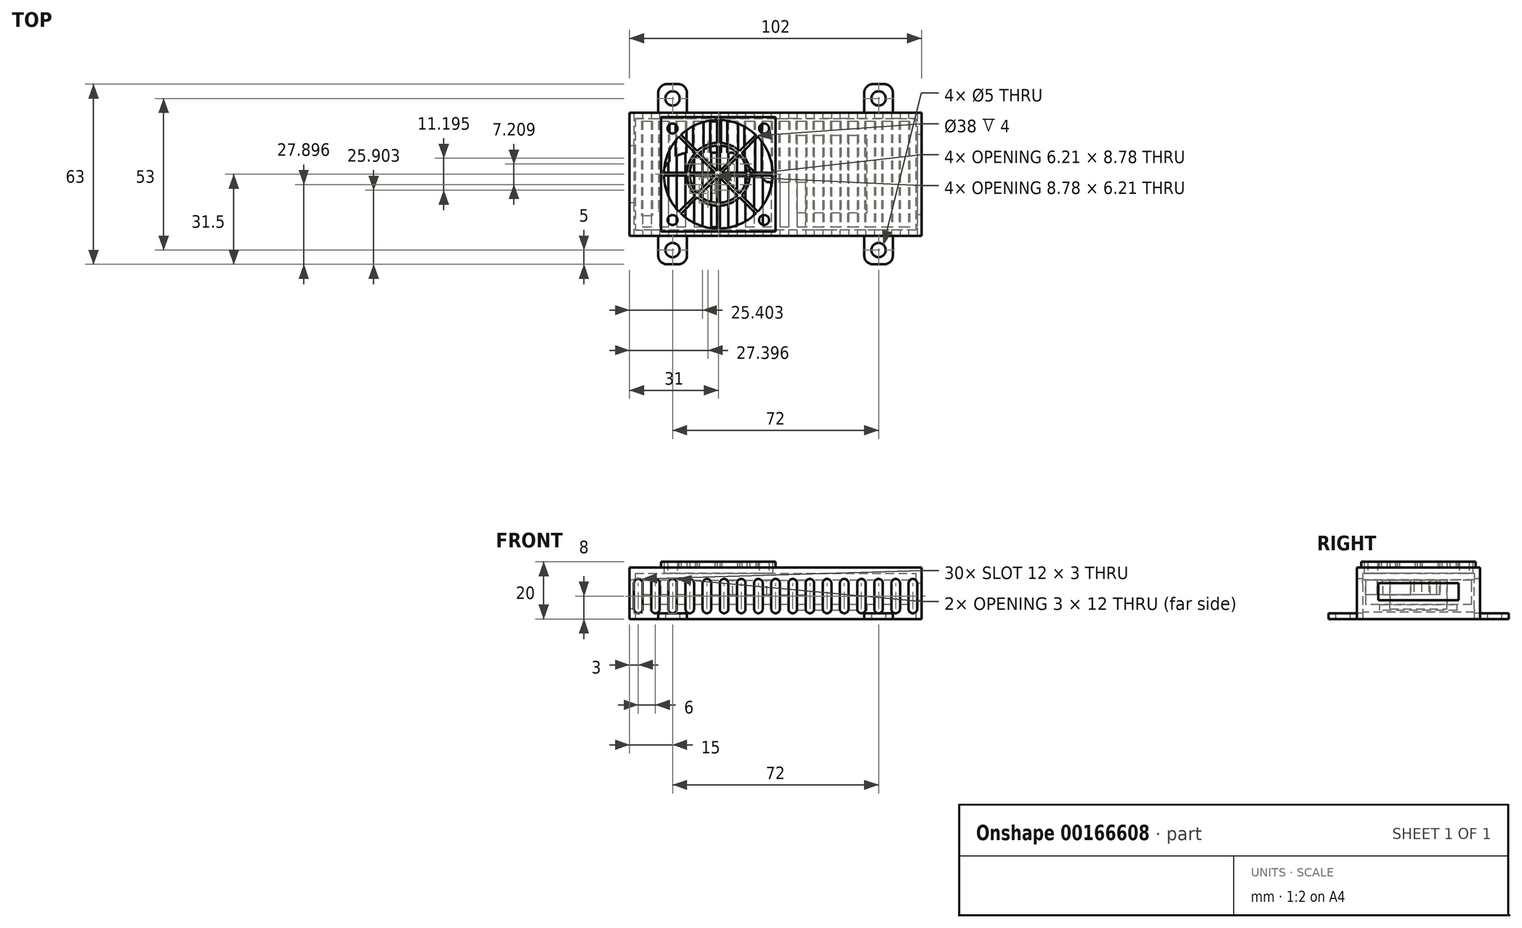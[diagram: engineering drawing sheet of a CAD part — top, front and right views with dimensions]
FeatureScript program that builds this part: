
annotation { "Feature Type Name" : "Feature", "Feature Type Description" : "" }
export const myFeature = defineFeature(function(context is Context, id is Id, definition is map)
    precondition{}
    {
        {
            var Q0;
            Q0=qCreatedBy(makeId("Top.planeOp"),FACE);
            cPlane(context, id + "F0", {"entities" : qUnion([Q0]), "cplaneType" : CPlaneType.OFFSET, "offset" : 5 * mm, "oppositeDirection" : true, "width" : 150 * mm, "height" : 150 * mm});
        }
        {
            var Q0;
            Q0=qCreatedBy(makeId("Top.planeOp"),FACE);
            var sketch = newSketch(context, id + "F1", { "sketchPlane" : qUnion([Q0])});
            skLineSegment(sketch, "E0.bottom", {"start": v(48, 18.5) * mm, "end": v(-48, 18.5) * mm});
            skLineSegment(sketch, "E0.top", {"start": v(48, -18.5) * mm, "end": v(-48, -18.5) * mm});
            skLineSegment(sketch, "E0.left", {"start": v(48, 18.5) * mm, "end": v(48, -18.5) * mm});
            skLineSegment(sketch, "E0.right", {"start": v(-48, 18.5) * mm, "end": v(-48, -18.5) * mm});
            skPoint(sketch, "E0.middle", {"position": v(0, 0) * mm});
            skSolve(sketch);
        }
        {
            var Q0;
            Q0 = qSketchRegion(id + "F1", true);
            extrude(context, id + "F2", {"entities" : qUnion([Q0]), "depth" : 8.5 * mm});
        }
        {
            var Q0;
            Q0=makeQuery(id+"F2.opExtrude","CAP_FACE",FACE,{"disambiguationData":[OSD([sQuery(id+"F1.wireOp",EDGE,"E0.bottom"),sQuery(id+"F1.wireOp",EDGE,"E0.top"),sQuery(id+"F1.wireOp",EDGE,"E0.left"),sQuery(id+"F1.wireOp",EDGE,"E0.right")])],"isStart":false});
            var sketch = newSketch(context, id + "F3", { "sketchPlane" : qUnion([Q0])});
            skLineSegment(sketch, "E1", {"start": v(-48, -14.5) * mm, "end": v(-44, -14.5) * mm});
            skLineSegment(sketch, "E2", {"start": v(-40, -10.5) * mm, "end": v(-40, -2.5) * mm});
            skLineSegment(sketch, "E3", {"start": v(-30, 7.5) * mm, "end": v(-15, 7.5) * mm});
            skLineSegment(sketch, "E4", {"start": v(-15, 7.5) * mm, "end": v(-3.1, -2.8) * mm});
            skLineSegment(sketch, "E5", {"start": v(-3.1, -2.8) * mm, "end": v(10.4, -2.8) * mm});
            skLineSegment(sketch, "E6", {"start": v(10.4, -2.8) * mm, "end": v(10.4, -18.5) * mm});
            skLineSegment(sketch, "E7", {"start": v(10.4, -18.5) * mm, "end": v(-48, -18.5) * mm});
            skLineSegment(sketch, "E8", {"start": v(-48, -18.5) * mm, "end": v(-48, -14.5) * mm});
            skPoint(sketch, "E9.visualSharp", {"position": v(-40, 7.5) * mm});
            skArc(sketch, "E9.filletArc", {"start": v(-30, 7.5) * mm, "mid": v(-37.07, 4.57) * mm, "end": v(-40, -2.5) * mm});
            skPoint(sketch, "E10.visualSharp", {"position": v(-40, -14.5) * mm});
            skArc(sketch, "E10.filletArc", {"start": v(-44, -14.5) * mm, "mid": v(-41.17, -13.33) * mm, "end": v(-40, -10.5) * mm});
            skSolve(sketch);
        }
        {
            var Q0;
            Q0 = qSketchRegion(id + "F3", true);
            extrude(context, id + "F4", {"entities" : qUnion([Q0]), "operationType" : NewBodyOperationType.REMOVE, "oppositeDirection" : true, "depth" : 5 * mm});
        }
        {
            var Q0;
            Q0=makeQuery(id+"F2.opExtrude","CAP_FACE",FACE,{"disambiguationData":[OSD([sQuery(id+"F1.wireOp",EDGE,"E0.bottom"),sQuery(id+"F1.wireOp",EDGE,"E0.top"),sQuery(id+"F1.wireOp",EDGE,"E0.left"),sQuery(id+"F1.wireOp",EDGE,"E0.right")])],"isStart":true});
            var sketch = newSketch(context, id + "F5", { "sketchPlane" : qUnion([Q0])});
            skLineSegment(sketch, "E11.bottom", {"start": v(32, 13.5) * mm, "end": v(5, 13.5) * mm});
            skLineSegment(sketch, "E11.top", {"start": v(32, -13.5) * mm, "end": v(5, -13.5) * mm});
            skLineSegment(sketch, "E11.left", {"start": v(32, 13.5) * mm, "end": v(32, -13.5) * mm});
            skLineSegment(sketch, "E11.right", {"start": v(5, 13.5) * mm, "end": v(5, -13.5) * mm});
            skPoint(sketch, "E11.middle", {"position": v(18.5, 0) * mm});
            skSolve(sketch);
        }
        {
            var Q0;
            Q0 = qSketchRegion(id + "F5", true);
            extrude(context, id + "F6", {"entities" : qUnion([Q0]), "operationType" : NewBodyOperationType.ADD, "depth" : 2 * mm});
        }
        {
            var Q0;
            Q0=qCreatedBy(id+"F0.planeOp",FACE);
            var sketch = newSketch(context, id + "F7", { "sketchPlane" : qUnion([Q0])});
            skLineSegment(sketch, "E12.0.0", {"start": v(48, 18.5) * mm, "end": v(48, -18.5) * mm, "construction": true});
            skLineSegment(sketch, "E12.0.1", {"start": v(48, -18.5) * mm, "end": v(-48, -18.5) * mm, "construction": true});
            skLineSegment(sketch, "E12.0.2", {"start": v(-48, -18.5) * mm, "end": v(-48, 18.5) * mm, "construction": true});
            skLineSegment(sketch, "E12.0.3", {"start": v(-48, 18.5) * mm, "end": v(48, 18.5) * mm, "construction": true});
            skLineSegment(sketch, "E13.0", {"start": v(-49, 19.5) * mm, "end": v(49, 19.5) * mm});
            skLineSegment(sketch, "E13.1", {"start": v(-49, -19.5) * mm, "end": v(-49, 19.5) * mm});
            skLineSegment(sketch, "E13.2", {"start": v(49, -19.5) * mm, "end": v(-49, -19.5) * mm});
            skLineSegment(sketch, "E13.3", {"start": v(49, 19.5) * mm, "end": v(49, -19.5) * mm});
            skLineSegment(sketch, "E14.0", {"start": v(-51, -21.5) * mm, "end": v(-51, 21.5) * mm});
            skLineSegment(sketch, "E14.1", {"start": v(51, -21.5) * mm, "end": v(-51, -21.5) * mm});
            skLineSegment(sketch, "E14.2", {"start": v(51, 21.5) * mm, "end": v(51, -21.5) * mm});
            skLineSegment(sketch, "E14.3", {"start": v(-51, 21.5) * mm, "end": v(51, 21.5) * mm});
            skSolve(sketch);
        }
        {
            var Q0;
            Q0 = qSketchRegion(id + "F7", true);
            var Q1;
            Q1=makeQuery(id+"F2.opExtrude","CAP_FACE",FACE,{"disambiguationData":[OSD([sQuery(id+"F1.wireOp",EDGE,"E0.bottom"),sQuery(id+"F1.wireOp",EDGE,"E0.top"),sQuery(id+"F1.wireOp",EDGE,"E0.left"),sQuery(id+"F1.wireOp",EDGE,"E0.right")])],"isStart":false});
            extrude(context, id + "F8", {"entities" : qUnion([Q0]), "endBoundEntityFace" : qUnion([Q1]), "depth" : 16 * mm});
        }
        {
            var Q0;
            Q0=makeQuery(id+"F8.opExtrude","SWEPT_FACE",FACE,{"disambiguationData":[OSD([sQuery(id+"F7.wireOp",EDGE,"E14.1")])]});
            var sketch = newSketch(context, id + "F9", { "sketchPlane" : qUnion([Q0])});
            skLineSegment(sketch, "E15", {"start": v(-51, 3) * mm, "end": v(51, 3) * mm, "construction": true});
            skLineSegment(sketch, "E16", {"start": v(0, 0) * mm, "end": v(0, 6) * mm, "construction": true});
            skLineSegment(sketch, "E17.bottom", {"start": v(0, 9) * mm, "end": v(0, 9) * mm});
            skLineSegment(sketch, "E17.top", {"start": v(0, -3) * mm, "end": v(0, -3) * mm});
            skLineSegment(sketch, "E17.left", {"start": v(1.5, 7.5) * mm, "end": v(1.5, -1.5) * mm});
            skLineSegment(sketch, "E17.right", {"start": v(-1.5, 7.5) * mm, "end": v(-1.5, -1.5) * mm});
            skPoint(sketch, "E17.middle", {"position": v(0, 3) * mm});
            skPoint(sketch, "E18.visualSharp", {"position": v(-1.5, 9) * mm});
            skArc(sketch, "E18.filletArc", {"start": v(0, 9) * mm, "mid": v(-1.06, 8.56) * mm, "end": v(-1.5, 7.5) * mm});
            skPoint(sketch, "E19.visualSharp", {"position": v(1.5, 9) * mm});
            skArc(sketch, "E19.filletArc", {"start": v(1.5, 7.5) * mm, "mid": v(1.06, 8.56) * mm, "end": v(0, 9) * mm});
            skPoint(sketch, "E20.visualSharp", {"position": v(1.5, -3) * mm});
            skArc(sketch, "E20.filletArc", {"start": v(0, -3) * mm, "mid": v(1.06, -2.56) * mm, "end": v(1.5, -1.5) * mm});
            skPoint(sketch, "E21.visualSharp", {"position": v(-1.5, -3) * mm});
            skArc(sketch, "E21.filletArc", {"start": v(-1.5, -1.5) * mm, "mid": v(-1.06, -2.56) * mm, "end": v(0, -3) * mm});
            skLineSegment(sketch, "E22.1.0.0", {"start": v(4.5, 7.5) * mm, "end": v(4.5, -1.5) * mm});
            skPoint(sketch, "E22.1.0.1", {"position": v(4.5, -3) * mm});
            skLineSegment(sketch, "E22.1.0.2", {"start": v(7.5, 7.5) * mm, "end": v(7.5, -1.5) * mm});
            skLineSegment(sketch, "E22.1.0.3", {"start": v(6, 0) * mm, "end": v(6, 6) * mm, "construction": true});
            skPoint(sketch, "E22.1.0.4", {"position": v(4.5, 9) * mm});
            skPoint(sketch, "E22.1.0.5", {"position": v(6, 3) * mm});
            skPoint(sketch, "E22.1.0.6", {"position": v(7.5, 9) * mm});
            skPoint(sketch, "E22.1.0.7", {"position": v(7.5, -3) * mm});
            skArc(sketch, "E22.1.0.8", {"start": v(7.5, 7.5) * mm, "mid": v(7.06, 8.56) * mm, "end": v(6, 9) * mm});
            skArc(sketch, "E22.1.0.9", {"start": v(6, 9) * mm, "mid": v(4.94, 8.56) * mm, "end": v(4.5, 7.5) * mm});
            skArc(sketch, "E22.1.0.10", {"start": v(6, -3) * mm, "mid": v(7.06, -2.56) * mm, "end": v(7.5, -1.5) * mm});
            skArc(sketch, "E22.1.0.11", {"start": v(4.5, -1.5) * mm, "mid": v(4.94, -2.56) * mm, "end": v(6, -3) * mm});
            skLineSegment(sketch, "E22.2.0.0", {"start": v(10.5, 7.5) * mm, "end": v(10.5, -1.5) * mm});
            skPoint(sketch, "E22.2.0.1", {"position": v(10.5, -3) * mm});
            skLineSegment(sketch, "E22.2.0.2", {"start": v(13.5, 7.5) * mm, "end": v(13.5, -1.5) * mm});
            skLineSegment(sketch, "E22.2.0.3", {"start": v(12, 0) * mm, "end": v(12, 6) * mm, "construction": true});
            skPoint(sketch, "E22.2.0.4", {"position": v(10.5, 9) * mm});
            skPoint(sketch, "E22.2.0.5", {"position": v(12, 3) * mm});
            skPoint(sketch, "E22.2.0.6", {"position": v(13.5, 9) * mm});
            skPoint(sketch, "E22.2.0.7", {"position": v(13.5, -3) * mm});
            skArc(sketch, "E22.2.0.8", {"start": v(13.5, 7.5) * mm, "mid": v(13.06, 8.56) * mm, "end": v(12, 9) * mm});
            skArc(sketch, "E22.2.0.9", {"start": v(12, 9) * mm, "mid": v(10.94, 8.56) * mm, "end": v(10.5, 7.5) * mm});
            skArc(sketch, "E22.2.0.10", {"start": v(12, -3) * mm, "mid": v(13.06, -2.56) * mm, "end": v(13.5, -1.5) * mm});
            skArc(sketch, "E22.2.0.11", {"start": v(10.5, -1.5) * mm, "mid": v(10.94, -2.56) * mm, "end": v(12, -3) * mm});
            skLineSegment(sketch, "E22.3.0.0", {"start": v(16.5, 7.5) * mm, "end": v(16.5, -1.5) * mm});
            skPoint(sketch, "E22.3.0.1", {"position": v(16.5, -3) * mm});
            skLineSegment(sketch, "E22.3.0.2", {"start": v(19.5, 7.5) * mm, "end": v(19.5, -1.5) * mm});
            skLineSegment(sketch, "E22.3.0.3", {"start": v(18, 0) * mm, "end": v(18, 6) * mm, "construction": true});
            skPoint(sketch, "E22.3.0.4", {"position": v(16.5, 9) * mm});
            skPoint(sketch, "E22.3.0.5", {"position": v(18, 3) * mm});
            skPoint(sketch, "E22.3.0.6", {"position": v(19.5, 9) * mm});
            skPoint(sketch, "E22.3.0.7", {"position": v(19.5, -3) * mm});
            skArc(sketch, "E22.3.0.8", {"start": v(19.5, 7.5) * mm, "mid": v(19.06, 8.56) * mm, "end": v(18, 9) * mm});
            skArc(sketch, "E22.3.0.9", {"start": v(18, 9) * mm, "mid": v(16.94, 8.56) * mm, "end": v(16.5, 7.5) * mm});
            skArc(sketch, "E22.3.0.10", {"start": v(18, -3) * mm, "mid": v(19.06, -2.56) * mm, "end": v(19.5, -1.5) * mm});
            skArc(sketch, "E22.3.0.11", {"start": v(16.5, -1.5) * mm, "mid": v(16.94, -2.56) * mm, "end": v(18, -3) * mm});
            skLineSegment(sketch, "E22.4.0.0", {"start": v(22.5, 7.5) * mm, "end": v(22.5, -1.5) * mm});
            skPoint(sketch, "E22.4.0.1", {"position": v(22.5, -3) * mm});
            skLineSegment(sketch, "E22.4.0.2", {"start": v(25.5, 7.5) * mm, "end": v(25.5, -1.5) * mm});
            skLineSegment(sketch, "E22.4.0.3", {"start": v(24, 0) * mm, "end": v(24, 6) * mm, "construction": true});
            skPoint(sketch, "E22.4.0.4", {"position": v(22.5, 9) * mm});
            skPoint(sketch, "E22.4.0.5", {"position": v(24, 3) * mm});
            skPoint(sketch, "E22.4.0.6", {"position": v(25.5, 9) * mm});
            skPoint(sketch, "E22.4.0.7", {"position": v(25.5, -3) * mm});
            skArc(sketch, "E22.4.0.8", {"start": v(25.5, 7.5) * mm, "mid": v(25.06, 8.56) * mm, "end": v(24, 9) * mm});
            skArc(sketch, "E22.4.0.9", {"start": v(24, 9) * mm, "mid": v(22.94, 8.56) * mm, "end": v(22.5, 7.5) * mm});
            skArc(sketch, "E22.4.0.10", {"start": v(24, -3) * mm, "mid": v(25.06, -2.56) * mm, "end": v(25.5, -1.5) * mm});
            skArc(sketch, "E22.4.0.11", {"start": v(22.5, -1.5) * mm, "mid": v(22.94, -2.56) * mm, "end": v(24, -3) * mm});
            skLineSegment(sketch, "E22.5.0.0", {"start": v(28.5, 7.5) * mm, "end": v(28.5, -1.5) * mm});
            skPoint(sketch, "E22.5.0.1", {"position": v(28.5, -3) * mm});
            skLineSegment(sketch, "E22.5.0.2", {"start": v(31.5, 7.5) * mm, "end": v(31.5, -1.5) * mm});
            skLineSegment(sketch, "E22.5.0.3", {"start": v(30, 0) * mm, "end": v(30, 6) * mm, "construction": true});
            skPoint(sketch, "E22.5.0.4", {"position": v(28.5, 9) * mm});
            skPoint(sketch, "E22.5.0.5", {"position": v(30, 3) * mm});
            skPoint(sketch, "E22.5.0.6", {"position": v(31.5, 9) * mm});
            skPoint(sketch, "E22.5.0.7", {"position": v(31.5, -3) * mm});
            skArc(sketch, "E22.5.0.8", {"start": v(31.5, 7.5) * mm, "mid": v(31.06, 8.56) * mm, "end": v(30, 9) * mm});
            skArc(sketch, "E22.5.0.9", {"start": v(30, 9) * mm, "mid": v(28.94, 8.56) * mm, "end": v(28.5, 7.5) * mm});
            skArc(sketch, "E22.5.0.10", {"start": v(30, -3) * mm, "mid": v(31.06, -2.56) * mm, "end": v(31.5, -1.5) * mm});
            skArc(sketch, "E22.5.0.11", {"start": v(28.5, -1.5) * mm, "mid": v(28.94, -2.56) * mm, "end": v(30, -3) * mm});
            skLineSegment(sketch, "E22.6.0.0", {"start": v(34.5, 7.5) * mm, "end": v(34.5, -1.5) * mm});
            skPoint(sketch, "E22.6.0.1", {"position": v(34.5, -3) * mm});
            skLineSegment(sketch, "E22.6.0.2", {"start": v(37.5, 7.5) * mm, "end": v(37.5, -1.5) * mm});
            skLineSegment(sketch, "E22.6.0.3", {"start": v(36, 0) * mm, "end": v(36, 6) * mm, "construction": true});
            skPoint(sketch, "E22.6.0.4", {"position": v(34.5, 9) * mm});
            skPoint(sketch, "E22.6.0.5", {"position": v(36, 3) * mm});
            skPoint(sketch, "E22.6.0.6", {"position": v(37.5, 9) * mm});
            skPoint(sketch, "E22.6.0.7", {"position": v(37.5, -3) * mm});
            skArc(sketch, "E22.6.0.8", {"start": v(37.5, 7.5) * mm, "mid": v(37.06, 8.56) * mm, "end": v(36, 9) * mm});
            skArc(sketch, "E22.6.0.9", {"start": v(36, 9) * mm, "mid": v(34.94, 8.56) * mm, "end": v(34.5, 7.5) * mm});
            skArc(sketch, "E22.6.0.10", {"start": v(36, -3) * mm, "mid": v(37.06, -2.56) * mm, "end": v(37.5, -1.5) * mm});
            skArc(sketch, "E22.6.0.11", {"start": v(34.5, -1.5) * mm, "mid": v(34.94, -2.56) * mm, "end": v(36, -3) * mm});
            skLineSegment(sketch, "E22.7.0.0", {"start": v(40.5, 7.5) * mm, "end": v(40.5, -1.5) * mm});
            skPoint(sketch, "E22.7.0.1", {"position": v(40.5, -3) * mm});
            skLineSegment(sketch, "E22.7.0.2", {"start": v(43.5, 7.5) * mm, "end": v(43.5, -1.5) * mm});
            skLineSegment(sketch, "E22.7.0.3", {"start": v(42, 0) * mm, "end": v(42, 6) * mm, "construction": true});
            skPoint(sketch, "E22.7.0.4", {"position": v(40.5, 9) * mm});
            skPoint(sketch, "E22.7.0.5", {"position": v(42, 3) * mm});
            skPoint(sketch, "E22.7.0.6", {"position": v(43.5, 9) * mm});
            skPoint(sketch, "E22.7.0.7", {"position": v(43.5, -3) * mm});
            skArc(sketch, "E22.7.0.8", {"start": v(43.5, 7.5) * mm, "mid": v(43.06, 8.56) * mm, "end": v(42, 9) * mm});
            skArc(sketch, "E22.7.0.9", {"start": v(42, 9) * mm, "mid": v(40.94, 8.56) * mm, "end": v(40.5, 7.5) * mm});
            skArc(sketch, "E22.7.0.10", {"start": v(42, -3) * mm, "mid": v(43.06, -2.56) * mm, "end": v(43.5, -1.5) * mm});
            skArc(sketch, "E22.7.0.11", {"start": v(40.5, -1.5) * mm, "mid": v(40.94, -2.56) * mm, "end": v(42, -3) * mm});
            skLineSegment(sketch, "E22.8.0.0", {"start": v(46.5, 7.5) * mm, "end": v(46.5, -1.5) * mm});
            skPoint(sketch, "E22.8.0.1", {"position": v(46.5, -3) * mm});
            skLineSegment(sketch, "E22.8.0.2", {"start": v(49.5, 7.5) * mm, "end": v(49.5, -1.5) * mm});
            skLineSegment(sketch, "E22.8.0.3", {"start": v(48, 0) * mm, "end": v(48, 6) * mm, "construction": true});
            skPoint(sketch, "E22.8.0.4", {"position": v(46.5, 9) * mm});
            skPoint(sketch, "E22.8.0.5", {"position": v(48, 3) * mm});
            skPoint(sketch, "E22.8.0.6", {"position": v(49.5, 9) * mm});
            skPoint(sketch, "E22.8.0.7", {"position": v(49.5, -3) * mm});
            skArc(sketch, "E22.8.0.8", {"start": v(49.5, 7.5) * mm, "mid": v(49.06, 8.56) * mm, "end": v(48, 9) * mm});
            skArc(sketch, "E22.8.0.9", {"start": v(48, 9) * mm, "mid": v(46.94, 8.56) * mm, "end": v(46.5, 7.5) * mm});
            skArc(sketch, "E22.8.0.10", {"start": v(48, -3) * mm, "mid": v(49.06, -2.56) * mm, "end": v(49.5, -1.5) * mm});
            skArc(sketch, "E22.8.0.11", {"start": v(46.5, -1.5) * mm, "mid": v(46.94, -2.56) * mm, "end": v(48, -3) * mm});
            skLineSegment(sketch, "E22.direction1", {"start": v(0, 0) * mm, "end": v(6, 0) * mm, "construction": true});
            skArc(sketch, "E23.MirrorCS", {"start": v(-6, 9) * mm, "mid": v(-4.94, 8.56) * mm, "end": v(-4.5, 7.5) * mm});
            skArc(sketch, "E24.MirrorCS", {"start": v(-7.5, 7.5) * mm, "mid": v(-7.06, 8.56) * mm, "end": v(-6, 9) * mm});
            skArc(sketch, "E25.MirrorCS", {"start": v(1.5, -1.5) * mm, "mid": v(1.06, -2.56) * mm, "end": v(0, -3) * mm});
            skArc(sketch, "E26.MirrorCS", {"start": v(0, -3) * mm, "mid": v(-1.06, -2.56) * mm, "end": v(-1.5, -1.5) * mm});
            skArc(sketch, "E27.MirrorCS", {"start": v(-1.5, 7.5) * mm, "mid": v(-1.06, 8.56) * mm, "end": v(0, 9) * mm});
            skArc(sketch, "E28.MirrorCS", {"start": v(0, 9) * mm, "mid": v(1.06, 8.56) * mm, "end": v(1.5, 7.5) * mm});
            skArc(sketch, "E29.MirrorCS", {"start": v(-4.5, -1.5) * mm, "mid": v(-4.94, -2.56) * mm, "end": v(-6, -3) * mm});
            skArc(sketch, "E30.MirrorCS", {"start": v(-6, -3) * mm, "mid": v(-7.06, -2.56) * mm, "end": v(-7.5, -1.5) * mm});
            skArc(sketch, "E31.MirrorCS", {"start": v(-46.5, -1.5) * mm, "mid": v(-46.94, -2.56) * mm, "end": v(-48, -3) * mm});
            skArc(sketch, "E32.MirrorCS", {"start": v(-42, 9) * mm, "mid": v(-40.94, 8.56) * mm, "end": v(-40.5, 7.5) * mm});
            skArc(sketch, "E33.MirrorCS", {"start": v(-36, 9) * mm, "mid": v(-34.94, 8.56) * mm, "end": v(-34.5, 7.5) * mm});
            skArc(sketch, "E34.MirrorCS", {"start": v(-48, -3) * mm, "mid": v(-49.06, -2.56) * mm, "end": v(-49.5, -1.5) * mm});
            skArc(sketch, "E35.MirrorCS", {"start": v(-10.5, -1.5) * mm, "mid": v(-10.94, -2.56) * mm, "end": v(-12, -3) * mm});
            skArc(sketch, "E36.MirrorCS", {"start": v(-37.5, 7.5) * mm, "mid": v(-37.06, 8.56) * mm, "end": v(-36, 9) * mm});
            skArc(sketch, "E37.MirrorCS", {"start": v(-43.5, 7.5) * mm, "mid": v(-43.06, 8.56) * mm, "end": v(-42, 9) * mm});
            skArc(sketch, "E38.MirrorCS", {"start": v(-49.5, 7.5) * mm, "mid": v(-49.06, 8.56) * mm, "end": v(-48, 9) * mm});
            skArc(sketch, "E39.MirrorCS", {"start": v(-16.5, -1.5) * mm, "mid": v(-16.94, -2.56) * mm, "end": v(-18, -3) * mm});
            skArc(sketch, "E40.MirrorCS", {"start": v(-48, 9) * mm, "mid": v(-46.94, 8.56) * mm, "end": v(-46.5, 7.5) * mm});
            skArc(sketch, "E41.MirrorCS", {"start": v(-12, -3) * mm, "mid": v(-13.06, -2.56) * mm, "end": v(-13.5, -1.5) * mm});
            skArc(sketch, "E42.MirrorCS", {"start": v(-18, -3) * mm, "mid": v(-19.06, -2.56) * mm, "end": v(-19.5, -1.5) * mm});
            skArc(sketch, "E43.MirrorCS", {"start": v(-12, 9) * mm, "mid": v(-10.94, 8.56) * mm, "end": v(-10.5, 7.5) * mm});
            skArc(sketch, "E44.MirrorCS", {"start": v(-22.5, -1.5) * mm, "mid": v(-22.94, -2.56) * mm, "end": v(-24, -3) * mm});
            skArc(sketch, "E45.MirrorCS", {"start": v(-28.5, -1.5) * mm, "mid": v(-28.94, -2.56) * mm, "end": v(-30, -3) * mm});
            skArc(sketch, "E46.MirrorCS", {"start": v(-18, 9) * mm, "mid": v(-16.94, 8.56) * mm, "end": v(-16.5, 7.5) * mm});
            skArc(sketch, "E47.MirrorCS", {"start": v(-13.5, 7.5) * mm, "mid": v(-13.06, 8.56) * mm, "end": v(-12, 9) * mm});
            skArc(sketch, "E48.MirrorCS", {"start": v(-24, -3) * mm, "mid": v(-25.06, -2.56) * mm, "end": v(-25.5, -1.5) * mm});
            skArc(sketch, "E49.MirrorCS", {"start": v(-30, -3) * mm, "mid": v(-31.06, -2.56) * mm, "end": v(-31.5, -1.5) * mm});
            skArc(sketch, "E50.MirrorCS", {"start": v(-19.5, 7.5) * mm, "mid": v(-19.06, 8.56) * mm, "end": v(-18, 9) * mm});
            skArc(sketch, "E51.MirrorCS", {"start": v(-30, 9) * mm, "mid": v(-28.94, 8.56) * mm, "end": v(-28.5, 7.5) * mm});
            skArc(sketch, "E52.MirrorCS", {"start": v(-40.5, -1.5) * mm, "mid": v(-40.94, -2.56) * mm, "end": v(-42, -3) * mm});
            skArc(sketch, "E53.MirrorCS", {"start": v(-24, 9) * mm, "mid": v(-22.94, 8.56) * mm, "end": v(-22.5, 7.5) * mm});
            skArc(sketch, "E54.MirrorCS", {"start": v(-42, -3) * mm, "mid": v(-43.06, -2.56) * mm, "end": v(-43.5, -1.5) * mm});
            skArc(sketch, "E55.MirrorCS", {"start": v(-36, -3) * mm, "mid": v(-37.06, -2.56) * mm, "end": v(-37.5, -1.5) * mm});
            skArc(sketch, "E56.MirrorCS", {"start": v(-34.5, -1.5) * mm, "mid": v(-34.94, -2.56) * mm, "end": v(-36, -3) * mm});
            skArc(sketch, "E57.MirrorCS", {"start": v(-31.5, 7.5) * mm, "mid": v(-31.06, 8.56) * mm, "end": v(-30, 9) * mm});
            skArc(sketch, "E58.MirrorCS", {"start": v(-25.5, 7.5) * mm, "mid": v(-25.06, 8.56) * mm, "end": v(-24, 9) * mm});
            skLineSegment(sketch, "E59.MirrorCS", {"start": v(-6, 0) * mm, "end": v(-6, 6) * mm, "construction": true});
            skLineSegment(sketch, "E60.MirrorCS", {"start": v(-7.5, 7.5) * mm, "end": v(-7.5, -1.5) * mm});
            skLineSegment(sketch, "E61.MirrorCS", {"start": v(-4.5, 7.5) * mm, "end": v(-4.5, -1.5) * mm});
            skLineSegment(sketch, "E62.MirrorCS", {"start": v(-10.5, 7.5) * mm, "end": v(-10.5, -1.5) * mm});
            skLineSegment(sketch, "E63.MirrorCS", {"start": v(-16.5, 7.5) * mm, "end": v(-16.5, -1.5) * mm});
            skLineSegment(sketch, "E64.MirrorCS", {"start": v(-24, 0) * mm, "end": v(-24, 6) * mm, "construction": true});
            skLineSegment(sketch, "E65.MirrorCS", {"start": v(-30, 0) * mm, "end": v(-30, 6) * mm, "construction": true});
            skPoint(sketch, "E66.MirrorP", {"position": v(-28.5, -3) * mm});
            skPoint(sketch, "E67.MirrorP", {"position": v(-7.5, -3) * mm});
            skPoint(sketch, "E68.MirrorP", {"position": v(-12, 3) * mm});
            skPoint(sketch, "E69.MirrorP", {"position": v(-22.5, -3) * mm});
            skPoint(sketch, "E70.MirrorP", {"position": v(-18, 3) * mm});
            skPoint(sketch, "E71.MirrorP", {"position": v(-37.5, -3) * mm});
            skPoint(sketch, "E72.MirrorP", {"position": v(-48, 3) * mm});
            skPoint(sketch, "E73.MirrorP", {"position": v(-4.5, 9) * mm});
            skLineSegment(sketch, "E74.MirrorCS", {"start": v(-31.5, 7.5) * mm, "end": v(-31.5, -1.5) * mm});
            skLineSegment(sketch, "E75.MirrorCS", {"start": v(-25.5, 7.5) * mm, "end": v(-25.5, -1.5) * mm});
            skLineSegment(sketch, "E76.MirrorCS", {"start": v(-37.5, 7.5) * mm, "end": v(-37.5, -1.5) * mm});
            skPoint(sketch, "E77.MirrorP", {"position": v(-43.5, -3) * mm});
            skPoint(sketch, "E78.MirrorP", {"position": v(-49.5, -3) * mm});
            skPoint(sketch, "E79.MirrorP", {"position": v(-10.5, 9) * mm});
            skPoint(sketch, "E80.MirrorP", {"position": v(-7.5, 9) * mm});
            skPoint(sketch, "E81.MirrorP", {"position": v(-16.5, 9) * mm});
            skPoint(sketch, "E82.MirrorP", {"position": v(-37.5, 9) * mm});
            skPoint(sketch, "E83.MirrorP", {"position": v(-46.5, 9) * mm});
            skPoint(sketch, "E84.MirrorP", {"position": v(-4.5, -3) * mm});
            skLineSegment(sketch, "E85.MirrorCS", {"start": v(-22.5, 7.5) * mm, "end": v(-22.5, -1.5) * mm});
            skLineSegment(sketch, "E86.MirrorCS", {"start": v(-28.5, 7.5) * mm, "end": v(-28.5, -1.5) * mm});
            skLineSegment(sketch, "E87.MirrorCS", {"start": v(-36, 0) * mm, "end": v(-36, 6) * mm, "construction": true});
            skLineSegment(sketch, "E88.MirrorCS", {"start": v(-42, 0) * mm, "end": v(-42, 6) * mm, "construction": true});
            skPoint(sketch, "E89.MirrorP", {"position": v(-43.5, 9) * mm});
            skPoint(sketch, "E90.MirrorP", {"position": v(-49.5, 9) * mm});
            skLineSegment(sketch, "E91.MirrorCS", {"start": v(-34.5, 7.5) * mm, "end": v(-34.5, -1.5) * mm});
            skLineSegment(sketch, "E92.MirrorCS", {"start": v(-48, 0) * mm, "end": v(-48, 6) * mm, "construction": true});
            skPoint(sketch, "E93.MirrorP", {"position": v(-6, 3) * mm});
            skPoint(sketch, "E94.MirrorP", {"position": v(-10.5, -3) * mm});
            skPoint(sketch, "E95.MirrorP", {"position": v(-16.5, -3) * mm});
            skLineSegment(sketch, "E96.MirrorCS", {"start": v(-43.5, 7.5) * mm, "end": v(-43.5, -1.5) * mm});
            skPoint(sketch, "E97.MirrorP", {"position": v(-31.5, -3) * mm});
            skPoint(sketch, "E98.MirrorP", {"position": v(-42, 3) * mm});
            skLineSegment(sketch, "E99.MirrorCS", {"start": v(-49.5, 7.5) * mm, "end": v(-49.5, -1.5) * mm});
            skPoint(sketch, "E100.MirrorP", {"position": v(-25.5, -3) * mm});
            skPoint(sketch, "E101.MirrorP", {"position": v(-36, 3) * mm});
            skPoint(sketch, "E102.MirrorP", {"position": v(-46.5, -3) * mm});
            skLineSegment(sketch, "E103.MirrorCS", {"start": v(-40.5, 7.5) * mm, "end": v(-40.5, -1.5) * mm});
            skPoint(sketch, "E104.MirrorP", {"position": v(-31.5, 9) * mm});
            skPoint(sketch, "E105.MirrorP", {"position": v(-40.5, 9) * mm});
            skLineSegment(sketch, "E106.MirrorCS", {"start": v(-46.5, 7.5) * mm, "end": v(-46.5, -1.5) * mm});
            skPoint(sketch, "E107.MirrorP", {"position": v(-25.5, 9) * mm});
            skPoint(sketch, "E108.MirrorP", {"position": v(-34.5, 9) * mm});
            skPoint(sketch, "E109.MirrorP", {"position": v(-30, 3) * mm});
            skPoint(sketch, "E110.MirrorP", {"position": v(-40.5, -3) * mm});
            skPoint(sketch, "E111.MirrorP", {"position": v(-19.5, -3) * mm});
            skLineSegment(sketch, "E112.MirrorCS", {"start": v(-18, 0) * mm, "end": v(-18, 6) * mm, "construction": true});
            skPoint(sketch, "E113.MirrorP", {"position": v(-13.5, -3) * mm});
            skPoint(sketch, "E114.MirrorP", {"position": v(-24, 3) * mm});
            skPoint(sketch, "E115.MirrorP", {"position": v(-34.5, -3) * mm});
            skLineSegment(sketch, "E116.MirrorCS", {"start": v(0, 0) * mm, "end": v(-6, 0) * mm, "construction": true});
            skLineSegment(sketch, "E117.MirrorCS", {"start": v(-12, 0) * mm, "end": v(-12, 6) * mm, "construction": true});
            skPoint(sketch, "E118.MirrorP", {"position": v(-28.5, 9) * mm});
            skLineSegment(sketch, "E119.MirrorCS", {"start": v(-13.5, 7.5) * mm, "end": v(-13.5, -1.5) * mm});
            skLineSegment(sketch, "E120.MirrorCS", {"start": v(-19.5, 7.5) * mm, "end": v(-19.5, -1.5) * mm});
            skPoint(sketch, "E121.MirrorP", {"position": v(-19.5, 9) * mm});
            skPoint(sketch, "E122.MirrorP", {"position": v(-13.5, 9) * mm});
            skPoint(sketch, "E123.MirrorP", {"position": v(-22.5, 9) * mm});
            skSolve(sketch);
        }
        {
            var Q0;
            Q0 = qSketchRegion(id + "F9", true);
            extrude(context, id + "F10", {"entities" : qUnion([Q0]), "operationType" : NewBodyOperationType.REMOVE, "endBound" : BoundingType.THROUGH_ALL, "oppositeDirection" : true, "depth" : 25 * mm});
        }
        {
            var Q0;
            Q0=makeQuery(id+"F8.opExtrude","SWEPT_FACE",FACE,{"disambiguationData":[OSD([sQuery(id+"F7.wireOp",EDGE,"E14.2")])]});
            var sketch = newSketch(context, id + "F11", { "sketchPlane" : qUnion([Q0])});
            skLineSegment(sketch, "E124", {"start": v(-21.5, 4.5) * mm, "end": v(21.5, 4.5) * mm, "construction": true});
            skLineSegment(sketch, "E125", {"start": v(0, 0) * mm, "end": v(0, 11) * mm, "construction": true});
            skLineSegment(sketch, "E126.bottom", {"start": v(14, 7.5) * mm, "end": v(-14, 7.5) * mm});
            skLineSegment(sketch, "E126.top", {"start": v(14, 1.5) * mm, "end": v(-14, 1.5) * mm});
            skLineSegment(sketch, "E126.left", {"start": v(14, 7.5) * mm, "end": v(14, 1.5) * mm});
            skLineSegment(sketch, "E126.right", {"start": v(-14, 7.5) * mm, "end": v(-14, 1.5) * mm});
            skPoint(sketch, "E126.middle", {"position": v(0, 4.5) * mm});
            skSolve(sketch);
        }
        {
            var Q0;
            Q0 = qSketchRegion(id + "F11", true);
            extrude(context, id + "F12", {"entities" : qUnion([Q0]), "operationType" : NewBodyOperationType.REMOVE, "endBound" : BoundingType.UP_TO_NEXT, "oppositeDirection" : true, "depth" : 25 * mm});
        }
        {
            var Q0;
            Q0=makeQuery(id+"F8.opExtrude","SWEPT_FACE",FACE,{"disambiguationData":[OSD([sQuery(id+"F7.wireOp",EDGE,"E14.0")])]});
            var sketch = newSketch(context, id + "F13", { "sketchPlane" : qUnion([Q0])});
            skLineSegment(sketch, "E127.bottom", {"start": v(10, -1.5) * mm, "end": v(-10, -1.5) * mm});
            skLineSegment(sketch, "E127.top", {"start": v(10, 8.5) * mm, "end": v(-10, 8.5) * mm});
            skLineSegment(sketch, "E127.left", {"start": v(10, -1.5) * mm, "end": v(10, 8.5) * mm});
            skLineSegment(sketch, "E127.right", {"start": v(-10, -1.5) * mm, "end": v(-10, 8.5) * mm});
            skPoint(sketch, "E127.middle", {"position": v(0, 3.5) * mm});
            skSolve(sketch);
        }
        {
            var Q0;
            Q0 = qSketchRegion(id + "F13", true);
            extrude(context, id + "F14", {"entities" : qUnion([Q0]), "operationType" : NewBodyOperationType.REMOVE, "endBound" : BoundingType.UP_TO_NEXT, "oppositeDirection" : true, "depth" : 25 * mm});
        }
        {
            var Q0;
            Q0=makeQuery(id+"F8.opExtrude","CAP_FACE",FACE,{"disambiguationData":[OSD([sQuery(id+"F7.wireOp",EDGE,"E13.0"),sQuery(id+"F7.wireOp",EDGE,"E13.1"),sQuery(id+"F7.wireOp",EDGE,"E13.2"),sQuery(id+"F7.wireOp",EDGE,"E13.3"),sQuery(id+"F7.wireOp",EDGE,"E14.0"),sQuery(id+"F7.wireOp",EDGE,"E14.1"),sQuery(id+"F7.wireOp",EDGE,"E14.2"),sQuery(id+"F7.wireOp",EDGE,"E14.3")])],"isStart":false});
            var sketch = newSketch(context, id + "F15", { "sketchPlane" : qUnion([Q0])});
            skLineSegment(sketch, "E128.0", {"start": v(-51, 21.5) * mm, "end": v(51, 21.5) * mm});
            skLineSegment(sketch, "E128.1", {"start": v(51, 21.5) * mm, "end": v(51, -21.5) * mm});
            skLineSegment(sketch, "E128.2", {"start": v(51, -21.5) * mm, "end": v(-51, -21.5) * mm});
            skLineSegment(sketch, "E128.3", {"start": v(-51, -21.5) * mm, "end": v(-51, 21.5) * mm});
            skCircle(sketch, "E129", {"center": v(-20, 0) * mm, "radius": 19 * mm});
            skLineSegment(sketch, "E130.bottom", {"start": v(-4, 16) * mm, "end": v(-36, 16) * mm, "construction": true});
            skLineSegment(sketch, "E130.top", {"start": v(-4, -16) * mm, "end": v(-36, -16) * mm, "construction": true});
            skLineSegment(sketch, "E130.left", {"start": v(-4, 16) * mm, "end": v(-4, -16) * mm, "construction": true});
            skLineSegment(sketch, "E130.right", {"start": v(-36, 16) * mm, "end": v(-36, -16) * mm, "construction": true});
            skCircle(sketch, "E131", {"center": v(-4, 16) * mm, "radius": 1.75 * mm});
            skCircle(sketch, "E132", {"center": v(-4, -16) * mm, "radius": 1.75 * mm});
            skCircle(sketch, "E133", {"center": v(-36, -16) * mm, "radius": 1.75 * mm});
            skCircle(sketch, "E134", {"center": v(-36, 16) * mm, "radius": 1.75 * mm});
            skSolve(sketch);
        }
        {
            var Q0;
            Q0 = qSketchRegion(id + "F15", true);
            extrude(context, id + "F16", {"entities" : qUnion([Q0]), "operationType" : NewBodyOperationType.ADD, "depth" : 2 * mm});
        }
        {
            var Q0;
            Q0=qCreatedBy(id+"F0.planeOp",FACE);
            var sketch = newSketch(context, id + "F17", { "sketchPlane" : qUnion([Q0])});
            skLineSegment(sketch, "E135.bottom", {"start": v(-41, -21.5) * mm, "end": v(-31, -21.5) * mm});
            skLineSegment(sketch, "E135.top", {"start": v(-38, -31.5) * mm, "end": v(-34, -31.5) * mm});
            skLineSegment(sketch, "E135.left", {"start": v(-41, -21.5) * mm, "end": v(-41, -28.5) * mm});
            skLineSegment(sketch, "E135.right", {"start": v(-31, -21.5) * mm, "end": v(-31, -28.5) * mm});
            skCircle(sketch, "E136", {"center": v(-36, -26.5) * mm, "radius": 2.5 * mm});
            skPoint(sketch, "E136.centerSnap0", {"position": v(-31, -26.5) * mm});
            skPoint(sketch, "E136.centerSnap1", {"position": v(-36, -31.5) * mm});
            skPoint(sketch, "E137.visualSharp", {"position": v(-41, -31.5) * mm});
            skArc(sketch, "E137.filletArc", {"start": v(-41, -28.5) * mm, "mid": v(-40.12, -30.62) * mm, "end": v(-38, -31.5) * mm});
            skPoint(sketch, "E138.visualSharp", {"position": v(-31, -31.5) * mm});
            skArc(sketch, "E138.filletArc", {"start": v(-34, -31.5) * mm, "mid": v(-31.88, -30.62) * mm, "end": v(-31, -28.5) * mm});
            skLineSegment(sketch, "E139", {"start": v(0, 0) * mm, "end": v(0, -40.28) * mm, "construction": true});
            skLineSegment(sketch, "E140", {"start": v(0, 0) * mm, "end": v(64.27, 0) * mm, "construction": true});
            skArc(sketch, "E141.MirrorCS", {"start": v(34, -31.5) * mm, "mid": v(31.88, -30.62) * mm, "end": v(31, -28.5) * mm});
            skArc(sketch, "E142.MirrorCS", {"start": v(41, -28.5) * mm, "mid": v(40.12, -30.62) * mm, "end": v(38, -31.5) * mm});
            skLineSegment(sketch, "E143.MirrorCS", {"start": v(38, -31.5) * mm, "end": v(34, -31.5) * mm});
            skLineSegment(sketch, "E144.MirrorCS", {"start": v(41, -21.5) * mm, "end": v(31, -21.5) * mm});
            skPoint(sketch, "E145.MirrorP", {"position": v(31, -26.5) * mm});
            skCircle(sketch, "E146.MirrorC", {"center": v(36, -26.5) * mm, "radius": 2.5 * mm});
            skPoint(sketch, "E147.MirrorP", {"position": v(31, -31.5) * mm});
            skPoint(sketch, "E148.MirrorP", {"position": v(41, -31.5) * mm});
            skLineSegment(sketch, "E149.MirrorCS", {"start": v(31, -21.5) * mm, "end": v(31, -28.5) * mm});
            skLineSegment(sketch, "E150.MirrorCS", {"start": v(41, -21.5) * mm, "end": v(41, -28.5) * mm});
            skPoint(sketch, "E151.MirrorP", {"position": v(36, -31.5) * mm});
            skArc(sketch, "E152.MirrorCS", {"start": v(34, 31.5) * mm, "mid": v(31.88, 30.62) * mm, "end": v(31, 28.5) * mm});
            skArc(sketch, "E153.MirrorCS", {"start": v(-41, 28.5) * mm, "mid": v(-40.12, 30.62) * mm, "end": v(-38, 31.5) * mm});
            skLineSegment(sketch, "E154.MirrorCS", {"start": v(38, 31.5) * mm, "end": v(34, 31.5) * mm});
            skArc(sketch, "E155.MirrorCS", {"start": v(-34, 31.5) * mm, "mid": v(-31.88, 30.62) * mm, "end": v(-31, 28.5) * mm});
            skArc(sketch, "E156.MirrorCS", {"start": v(41, 28.5) * mm, "mid": v(40.12, 30.62) * mm, "end": v(38, 31.5) * mm});
            skLineSegment(sketch, "E157.MirrorCS", {"start": v(-38, 31.5) * mm, "end": v(-34, 31.5) * mm});
            skLineSegment(sketch, "E158.MirrorCS", {"start": v(41, 21.5) * mm, "end": v(31, 21.5) * mm});
            skLineSegment(sketch, "E159.MirrorCS", {"start": v(-41, 21.5) * mm, "end": v(-31, 21.5) * mm});
            skLineSegment(sketch, "E160.MirrorCS", {"start": v(31, 21.5) * mm, "end": v(31, 28.5) * mm});
            skLineSegment(sketch, "E161.MirrorCS", {"start": v(-31, 21.5) * mm, "end": v(-31, 28.5) * mm});
            skLineSegment(sketch, "E162.MirrorCS", {"start": v(-41, 21.5) * mm, "end": v(-41, 28.5) * mm});
            skLineSegment(sketch, "E163.MirrorCS", {"start": v(41, 21.5) * mm, "end": v(41, 28.5) * mm});
            skPoint(sketch, "E164.MirrorP", {"position": v(31, 26.5) * mm});
            skPoint(sketch, "E165.MirrorP", {"position": v(-31, 26.5) * mm});
            skCircle(sketch, "E166.MirrorC", {"center": v(36, 26.5) * mm, "radius": 2.5 * mm});
            skCircle(sketch, "E167.MirrorC", {"center": v(-36, 26.5) * mm, "radius": 2.5 * mm});
            skPoint(sketch, "E168.MirrorP", {"position": v(41, 31.5) * mm});
            skPoint(sketch, "E169.MirrorP", {"position": v(36, 31.5) * mm});
            skPoint(sketch, "E170.MirrorP", {"position": v(31, 31.5) * mm});
            skPoint(sketch, "E171.MirrorP", {"position": v(-31, 31.5) * mm});
            skPoint(sketch, "E172.MirrorP", {"position": v(-36, 31.5) * mm});
            skPoint(sketch, "E173.MirrorP", {"position": v(-41, 31.5) * mm});
            skSolve(sketch);
        }
        {
            var Q0;
            Q0 = qSketchRegion(id + "F17", true);
            extrude(context, id + "F18", {"entities" : qUnion([Q0]), "operationType" : NewBodyOperationType.ADD, "depth" : 2 * mm});
        }
        {
            var Q0;
            Q0=makeQuery(id+"F16.opExtrude","CAP_FACE",FACE,{"disambiguationData":[OSD([sQuery(id+"F15.wireOp",EDGE,"E128.0"),sQuery(id+"F15.wireOp",EDGE,"E128.1"),sQuery(id+"F15.wireOp",EDGE,"E128.2"),sQuery(id+"F15.wireOp",EDGE,"E128.3"),sQuery(id+"F15.wireOp",EDGE,"E129"),sQuery(id+"F15.wireOp",EDGE,"E131"),sQuery(id+"F15.wireOp",EDGE,"E132"),sQuery(id+"F15.wireOp",EDGE,"E133"),sQuery(id+"F15.wireOp",EDGE,"E134")])],"isStart":false});
            var sketch = newSketch(context, id + "F19", { "sketchPlane" : qUnion([Q0])});
            skCircle(sketch, "E174.0", {"center": v(-4, 16) * mm, "radius": 1.75 * mm});
            skCircle(sketch, "E174.1", {"center": v(-36, 16) * mm, "radius": 1.75 * mm});
            skCircle(sketch, "E174.2", {"center": v(-36, -16) * mm, "radius": 1.75 * mm});
            skCircle(sketch, "E174.3", {"center": v(-4, -16) * mm, "radius": 1.75 * mm});
            skLineSegment(sketch, "E175.bottom", {"start": v(0, 20) * mm, "end": v(-40, 20) * mm});
            skLineSegment(sketch, "E175.top", {"start": v(0, -20) * mm, "end": v(-40, -20) * mm});
            skLineSegment(sketch, "E175.left", {"start": v(0, 20) * mm, "end": v(0, -20) * mm});
            skLineSegment(sketch, "E175.right", {"start": v(-40, 20) * mm, "end": v(-40, -20) * mm});
            skPoint(sketch, "E175.middle", {"position": v(-20, 0) * mm});
            skLineSegment(sketch, "E176", {"start": v(-20, 0) * mm, "end": v(-1, 0) * mm, "construction": true});
            skLineSegment(sketch, "E177.MirrorCS", {"start": v(-18.8, 0.5) * mm, "end": v(-10.01, 0.5) * mm});
            skLineSegment(sketch, "E178.1.1", {"start": v(-20, 0) * mm, "end": v(-6.56, 13.44) * mm, "construction": true});
            skLineSegment(sketch, "E178.2.0", {"start": v(-20.5, 1.2) * mm, "end": v(-20.5, 9.99) * mm});
            skLineSegment(sketch, "E178.2.1", {"start": v(-20, 0) * mm, "end": v(-20, 19) * mm, "construction": true});
            skLineSegment(sketch, "E178.3.1", {"start": v(-20, 0) * mm, "end": v(-33.44, 13.44) * mm, "construction": true});
            skLineSegment(sketch, "E178.3.2", {"start": v(-20.5, 1.2) * mm, "end": v(-26.7, 7.42) * mm});
            skLineSegment(sketch, "E178.4.1", {"start": v(-20, 0) * mm, "end": v(-39, 0) * mm, "construction": true});
            skLineSegment(sketch, "E178.4.2", {"start": v(-21.2, 0.5) * mm, "end": v(-29.99, 0.5) * mm});
            skLineSegment(sketch, "E178.5.0", {"start": v(-20.5, -1.2) * mm, "end": v(-26.7, -7.42) * mm});
            skLineSegment(sketch, "E178.5.1", {"start": v(-20, 0) * mm, "end": v(-33.44, -13.44) * mm, "construction": true});
            skLineSegment(sketch, "E178.6.0", {"start": v(-19.5, -1.2) * mm, "end": v(-19.5, -9.99) * mm});
            skLineSegment(sketch, "E178.6.1", {"start": v(-20, 0) * mm, "end": v(-20, -19) * mm, "construction": true});
            skLineSegment(sketch, "E178.7.1", {"start": v(-20, 0) * mm, "end": v(-6.56, -13.44) * mm, "construction": true});
            skArc(sketch, "E179", {"start": v(-12.58, -6.7) * mm, "mid": v(-10.76, -3.83) * mm, "end": v(-10.01, -0.5) * mm});
            skArc(sketch, "E180.0", {"start": v(-11.88, -7.42) * mm, "mid": v(-9.84, -4.2) * mm, "end": v(-9.01, -0.5) * mm});
            skArc(sketch, "E181.trimOffspring", {"start": v(-6.56, 13.44) * mm, "mid": v(-12.5, 17.46) * mm, "end": v(-19.5, 19) * mm});
            skArc(sketch, "E182.trimOffspring", {"start": v(-20.5, 19) * mm, "mid": v(-27.27, 17.55) * mm, "end": v(-33.08, 13.78) * mm});
            skArc(sketch, "E183.trimOffspring", {"start": v(-33.78, 13.08) * mm, "mid": v(-37.55, 7.27) * mm, "end": v(-39, 0.5) * mm});
            skArc(sketch, "E184.trimOffspring", {"start": v(-39, -0.5) * mm, "mid": v(-37.55, -7.27) * mm, "end": v(-33.78, -13.08) * mm});
            skArc(sketch, "E185.trimOffspring", {"start": v(-33.08, -13.78) * mm, "mid": v(-27.27, -17.55) * mm, "end": v(-20.5, -19) * mm});
            skArc(sketch, "E186.trimOffspring", {"start": v(-19.5, -19) * mm, "mid": v(-12.73, -17.55) * mm, "end": v(-6.92, -13.78) * mm});
            skArc(sketch, "E187.trimOffspring", {"start": v(-6.22, -13.08) * mm, "mid": v(-2.45, -7.27) * mm, "end": v(-1, -0.5) * mm});
            skLineSegment(sketch, "E188.trimOffspring", {"start": v(-11.88, -7.42) * mm, "end": v(-6.22, -13.08) * mm});
            skLineSegment(sketch, "E189.trimOffspring", {"start": v(-12.58, -8.12) * mm, "end": v(-6.92, -13.78) * mm});
            skLineSegment(sketch, "E190.trimOffspring", {"start": v(-19.5, -10.99) * mm, "end": v(-19.5, -19) * mm});
            skLineSegment(sketch, "E191.trimOffspring", {"start": v(-20.5, -10.99) * mm, "end": v(-20.5, -19) * mm});
            skArc(sketch, "E192.trimOffspring", {"start": v(-19.5, -9.99) * mm, "mid": v(-16.17, -9.24) * mm, "end": v(-13.3, -7.42) * mm});
            skArc(sketch, "E193.trimOffspring", {"start": v(-19.5, -10.99) * mm, "mid": v(-15.8, -10.16) * mm, "end": v(-12.58, -8.12) * mm});
            skArc(sketch, "E194.trimOffspring", {"start": v(-27.42, -8.12) * mm, "mid": v(-24.2, -10.16) * mm, "end": v(-20.5, -10.99) * mm});
            skArc(sketch, "E195.trimOffspring", {"start": v(-26.7, -7.42) * mm, "mid": v(-23.83, -9.24) * mm, "end": v(-20.5, -9.99) * mm});
            skLineSegment(sketch, "E196.trimOffspring", {"start": v(-27.42, -8.12) * mm, "end": v(-33.08, -13.78) * mm});
            skLineSegment(sketch, "E197.trimOffspring", {"start": v(-28.12, -7.42) * mm, "end": v(-33.78, -13.08) * mm});
            skLineSegment(sketch, "E198.trimOffspring", {"start": v(-30.99, -0.5) * mm, "end": v(-39, -0.5) * mm});
            skArc(sketch, "E199.trimOffspring", {"start": v(-29.99, -0.5) * mm, "mid": v(-29.24, -3.83) * mm, "end": v(-27.42, -6.7) * mm});
            skArc(sketch, "E200.trimOffspring", {"start": v(-30.99, -0.5) * mm, "mid": v(-30.16, -4.2) * mm, "end": v(-28.12, -7.42) * mm});
            skLineSegment(sketch, "E201.trimOffspring", {"start": v(-30.99, 0.5) * mm, "end": v(-39, 0.5) * mm});
            skLineSegment(sketch, "E202.trimOffspring", {"start": v(-9.01, 0.5) * mm, "end": v(-1, 0.5) * mm});
            skLineSegment(sketch, "E203.trimOffspring", {"start": v(-9.01, -0.5) * mm, "end": v(-1, -0.5) * mm});
            skArc(sketch, "E204.trimOffspring", {"start": v(-10.01, 0.5) * mm, "mid": v(-10.76, 3.83) * mm, "end": v(-12.58, 6.7) * mm});
            skArc(sketch, "E205.trimOffspring", {"start": v(-9.01, 0.5) * mm, "mid": v(-9.84, 4.2) * mm, "end": v(-11.88, 7.42) * mm});
            skLineSegment(sketch, "E206.trimOffspring", {"start": v(-11.88, 7.42) * mm, "end": v(-6.22, 13.08) * mm});
            skLineSegment(sketch, "E207.trimOffspring", {"start": v(-12.58, 8.12) * mm, "end": v(-6.92, 13.78) * mm});
            skArc(sketch, "E208.trimOffspring", {"start": v(-12.58, 8.12) * mm, "mid": v(-15.8, 10.16) * mm, "end": v(-19.5, 10.99) * mm});
            skArc(sketch, "E209.trimOffspring", {"start": v(-13.3, 7.42) * mm, "mid": v(-16.17, 9.24) * mm, "end": v(-19.5, 9.99) * mm});
            skArc(sketch, "E210.trimOffspring", {"start": v(-20.5, 10.99) * mm, "mid": v(-24.2, 10.16) * mm, "end": v(-27.42, 8.12) * mm});
            skLineSegment(sketch, "E211.trimOffspring", {"start": v(-20.5, 10.99) * mm, "end": v(-20.5, 19) * mm});
            skLineSegment(sketch, "E212.trimOffspring", {"start": v(-19.5, 10.99) * mm, "end": v(-19.5, 19) * mm});
            skArc(sketch, "E213.trimOffspring", {"start": v(-20.5, 9.99) * mm, "mid": v(-23.83, 9.24) * mm, "end": v(-26.7, 7.42) * mm});
            skLineSegment(sketch, "E214.trimOffspring", {"start": v(-27.42, 8.12) * mm, "end": v(-33.08, 13.78) * mm});
            skLineSegment(sketch, "E215.trimOffspring", {"start": v(-28.12, 7.42) * mm, "end": v(-33.78, 13.08) * mm});
            skArc(sketch, "E216.trimOffspring", {"start": v(-27.42, 6.7) * mm, "mid": v(-29.24, 3.83) * mm, "end": v(-29.99, 0.5) * mm});
            skArc(sketch, "E217.trimOffspring", {"start": v(-28.12, 7.42) * mm, "mid": v(-30.16, 4.2) * mm, "end": v(-30.99, 0.5) * mm});
            skLineSegment(sketch, "E218.trimOffspring", {"start": v(-18.8, 0.5) * mm, "end": v(-12.58, 6.7) * mm});
            skPoint(sketch, "E219.orphan", {"position": v(-19.5, 0) * mm});
            skLineSegment(sketch, "E220.trimOffspring", {"start": v(-18.8, -0.5) * mm, "end": v(-12.58, -6.7) * mm});
            skPoint(sketch, "E221.orphan", {"position": v(-19.65, 0.35) * mm});
            skLineSegment(sketch, "E222.trimOffspring", {"start": v(-19.5, 1.2) * mm, "end": v(-13.3, 7.42) * mm});
            skPoint(sketch, "E223.orphan", {"position": v(-20, 0.5) * mm});
            skLineSegment(sketch, "E224.trimOffspring", {"start": v(-19.5, 1.2) * mm, "end": v(-19.5, 9.99) * mm});
            skPoint(sketch, "E225.orphan", {"position": v(-19.65, -0.35) * mm});
            skLineSegment(sketch, "E226.trimOffspring", {"start": v(-18.8, -0.5) * mm, "end": v(-10.01, -0.5) * mm});
            skLineSegment(sketch, "E227.trimOffspring", {"start": v(-19.5, -1.2) * mm, "end": v(-13.3, -7.42) * mm});
            skPoint(sketch, "E228.0.start.orphan", {"position": v(-20, -0.5) * mm});
            skLineSegment(sketch, "E229.trimOffspring", {"start": v(-20.5, -1.2) * mm, "end": v(-20.5, -9.99) * mm});
            skLineSegment(sketch, "E230.trimOffspring", {"start": v(-21.2, -0.5) * mm, "end": v(-29.99, -0.5) * mm});
            skLineSegment(sketch, "E231.trimOffspring", {"start": v(-21.2, 0.5) * mm, "end": v(-27.42, 6.7) * mm});
            skLineSegment(sketch, "E232.trimOffspring", {"start": v(-21.2, -0.5) * mm, "end": v(-27.42, -6.7) * mm});
            skPoint(sketch, "E233.orphan", {"position": v(-20.5, 0) * mm});
            skArc(sketch, "E234", {"start": v(-1, 0.5) * mm, "mid": v(-2.45, 7.27) * mm, "end": v(-6.22, 13.08) * mm});
            skSolve(sketch);
        }
        {
            var Q0;
            Q0 = qSketchRegion(id + "F19", true);
            extrude(context, id + "F20", {"entities" : qUnion([Q0]), "operationType" : NewBodyOperationType.ADD, "depth" : 2 * mm});
        }
    });
